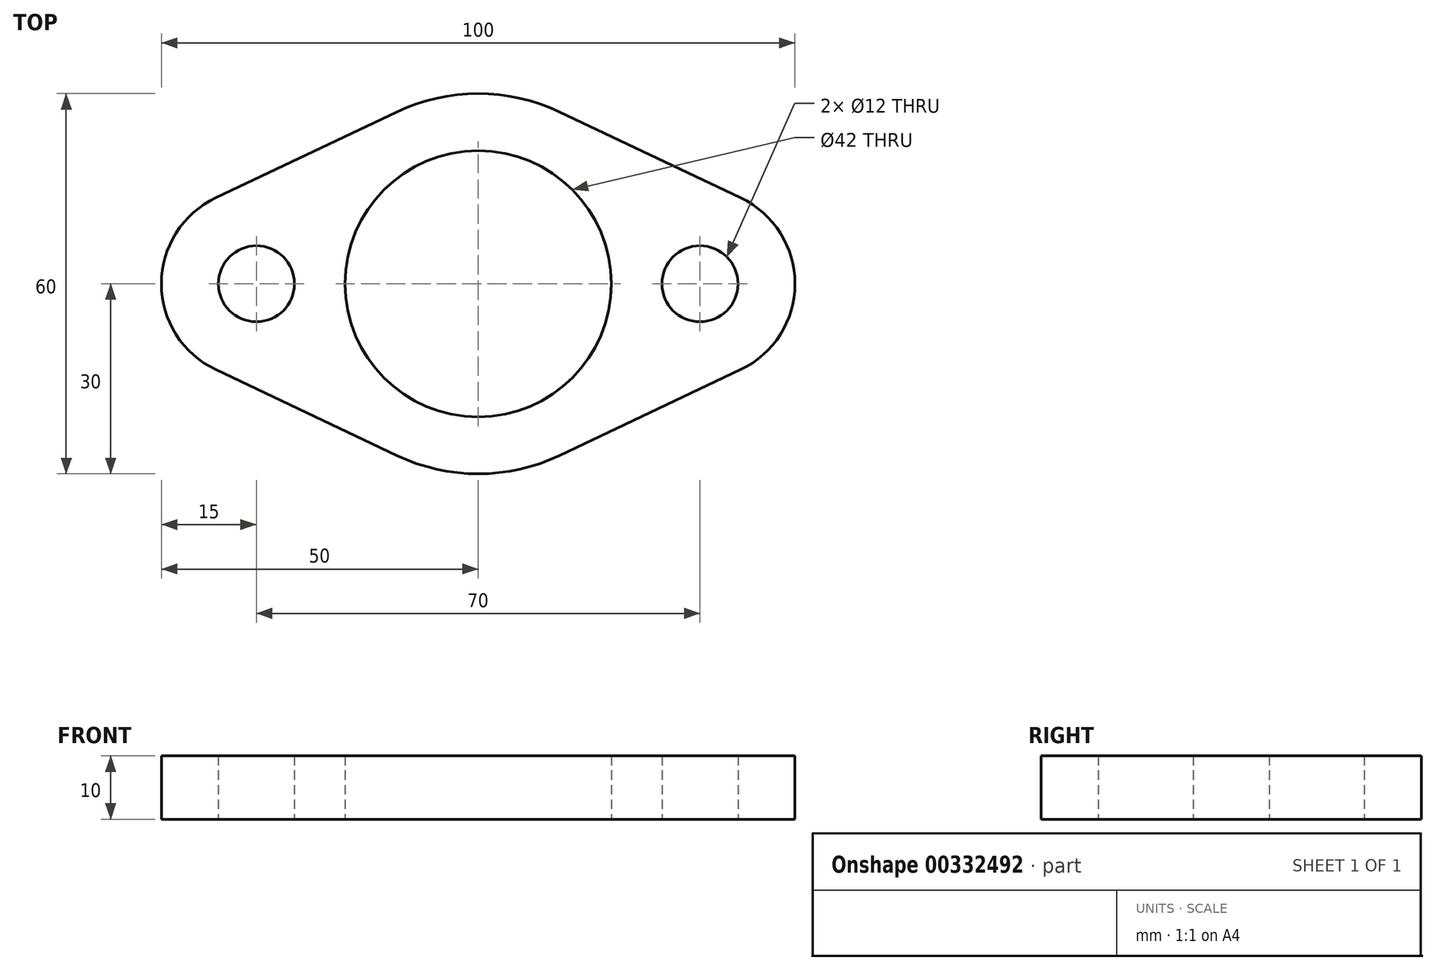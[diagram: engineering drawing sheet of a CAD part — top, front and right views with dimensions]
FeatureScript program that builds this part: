
annotation { "Feature Type Name" : "Feature", "Feature Type Description" : "" }
export const myFeature = defineFeature(function(context is Context, id is Id, definition is map)
    precondition{}
    {
        {
            var Q0;
            Q0=qCreatedBy(makeId("Top.planeOp"),FACE);
            var sketch = newSketch(context, id + "F0", { "sketchPlane" : qUnion([Q0])});
            skCircle(sketch, "E0", {"center": v(0, 0) * mm, "radius": 21 * mm});
            skPoint(sketch, "E1", {"position": v(-35, 0) * mm});
            skCircle(sketch, "E2", {"center": v(-35, 0) * mm, "radius": 6 * mm});
            skArc(sketch, "E3", {"start": v(-41.43, 13.55) * mm, "mid": v(-50, 0) * mm, "end": v(-41.43, -13.55) * mm});
            skCircle(sketch, "E4.MirrorC", {"center": v(35, 0) * mm, "radius": 6 * mm});
            skArc(sketch, "E5.MirrorC", {"start": v(41.43, 13.55) * mm, "mid": v(50, 0) * mm, "end": v(41.43, -13.55) * mm});
            skLineSegment(sketch, "E6", {"start": v(-41.43, 13.55) * mm, "end": v(-12.86, 27.1) * mm});
            skLineSegment(sketch, "E7.MirrorCS", {"start": v(-41.43, -13.55) * mm, "end": v(-12.86, -27.1) * mm});
            skLineSegment(sketch, "E8.MirrorCS", {"start": v(41.43, 13.55) * mm, "end": v(12.86, 27.1) * mm});
            skLineSegment(sketch, "E9.MirrorCS", {"start": v(41.43, -13.55) * mm, "end": v(12.86, -27.1) * mm});
            skArc(sketch, "E10.trimOffspring", {"start": v(12.86, 27.1) * mm, "mid": v(0, 30) * mm, "end": v(-12.86, 27.1) * mm});
            skArc(sketch, "E11.trimOffspring", {"start": v(-12.86, -27.1) * mm, "mid": v(0, -30) * mm, "end": v(12.86, -27.1) * mm});
            skSolve(sketch);
        }
        {
            var Q0;
            Q0 = qSketchRegion(id + "F0", true);
            extrude(context, id + "F1", {"entities" : qUnion([Q0]), "depth" : 10 * mm});
        }
    });
